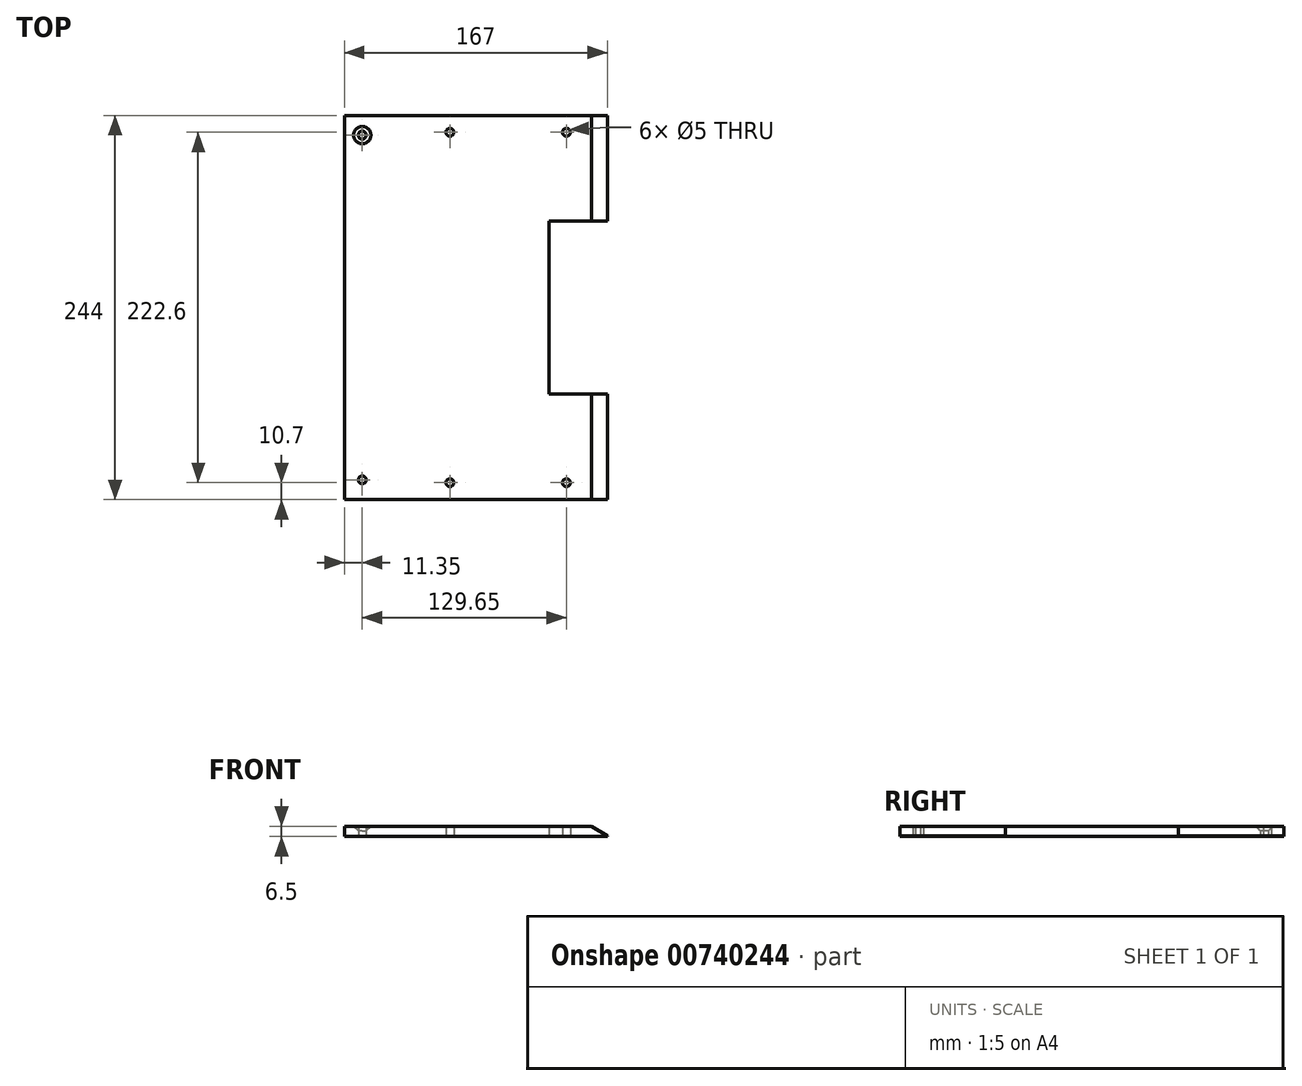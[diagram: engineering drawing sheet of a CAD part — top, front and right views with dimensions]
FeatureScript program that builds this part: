
annotation { "Feature Type Name" : "Feature", "Feature Type Description" : "" }
export const myFeature = defineFeature(function(context is Context, id is Id, definition is map)
    precondition{}
    {
        {
            var Q0;
            Q0=qCreatedBy(makeId("Top.planeOp"),FACE);
            var sketch = newSketch(context, id + "F0", { "sketchPlane" : qUnion([Q0])});
            skLineSegment(sketch, "E0.bottom", {"start": v(-120, 81) * mm, "end": v(-55, 81) * mm});
            skLineSegment(sketch, "E0.top", {"start": v(-120, -81) * mm, "end": v(120, -81) * mm});
            skLineSegment(sketch, "E0.left", {"start": v(-120, 81) * mm, "end": v(-120, -81) * mm});
            skLineSegment(sketch, "E0.right", {"start": v(120, 81) * mm, "end": v(120, -81) * mm});
            skLineSegment(sketch, "E1", {"start": v(-109, 81) * mm, "end": v(-109, -81) * mm, "construction": true});
            skLineSegment(sketch, "E2", {"start": v(109, 81) * mm, "end": v(109, -81) * mm, "construction": true});
            skCircle(sketch, "E3", {"center": v(-109, -74.65) * mm, "radius": 2.5 * mm});
            skCircle(sketch, "E4", {"center": v(-109, -19) * mm, "radius": 2.5 * mm});
            skCircle(sketch, "E5", {"center": v(-109, 55) * mm, "radius": 2.5 * mm});
            skCircle(sketch, "E6.MirrorC", {"center": v(109, 55) * mm, "radius": 2.5 * mm});
            skCircle(sketch, "E7.MirrorC", {"center": v(109, -19) * mm, "radius": 2.5 * mm});
            skCircle(sketch, "E8.MirrorC", {"center": v(109, -74.65) * mm, "radius": 2.5 * mm});
            skLineSegment(sketch, "E9.top", {"start": v(-55, 44) * mm, "end": v(55, 44) * mm});
            skLineSegment(sketch, "E9.left", {"start": v(-55, 81) * mm, "end": v(-55, 44) * mm});
            skLineSegment(sketch, "E9.right", {"start": v(55, 81) * mm, "end": v(55, 44) * mm});
            skLineSegment(sketch, "E10.trimOffspring", {"start": v(55, 81) * mm, "end": v(120, 81) * mm});
            skSolve(sketch);
        }
        {
            var Q0;
            Q0=qCreatedBy(makeId("Top.planeOp"),FACE);
            cPlane(context, id + "F1", {"entities" : qUnion([Q0]), "cplaneType" : CPlaneType.OFFSET, "offset" : 3.25 * mm, "width" : 150 * mm, "height" : 150 * mm});
        }
        {
            var Q0;
            Q0=qCreatedBy(id+"F1.planeOp",FACE);
            var sketch = newSketch(context, id + "F2", { "sketchPlane" : qUnion([Q0])});
            skLineSegment(sketch, "E11.0", {"start": v(-120, -81) * mm, "end": v(120, -81) * mm});
            skLineSegment(sketch, "E12.0", {"start": v(-120, 81) * mm, "end": v(-120, -81) * mm});
            skPoint(sketch, "E13.0", {"position": v(-87.5, 81) * mm});
            skLineSegment(sketch, "E14.0", {"start": v(-120, 81) * mm, "end": v(-55, 81) * mm});
            skLineSegment(sketch, "E15.0", {"start": v(-55, 81) * mm, "end": v(-55, 44) * mm});
            skLineSegment(sketch, "E16.0", {"start": v(-55, 44) * mm, "end": v(55, 44) * mm});
            skLineSegment(sketch, "E17.0", {"start": v(55, 81) * mm, "end": v(55, 44) * mm});
            skLineSegment(sketch, "E18.0", {"start": v(55, 81) * mm, "end": v(120, 81) * mm});
            skLineSegment(sketch, "E19.0", {"start": v(120, 81) * mm, "end": v(120, -81) * mm});
            skCircle(sketch, "E20.0", {"center": v(-109, 55) * mm, "radius": 2.5 * mm, "construction": true});
            skCircle(sketch, "E21.0", {"center": v(-109, -19) * mm, "radius": 2.5 * mm, "construction": true});
            skCircle(sketch, "E22.0", {"center": v(-109, -74.65) * mm, "radius": 2.5 * mm, "construction": true});
            skCircle(sketch, "E23.0", {"center": v(109, -74.65) * mm, "radius": 2.5 * mm, "construction": true});
            skCircle(sketch, "E24.0", {"center": v(109, -19) * mm, "radius": 2.5 * mm, "construction": true});
            skCircle(sketch, "E25.0", {"center": v(109, 55) * mm, "radius": 2.5 * mm, "construction": true});
            skCircle(sketch, "E26", {"center": v(-109, 55) * mm, "radius": 5.25 * mm});
            skCircle(sketch, "E27", {"center": v(-109, -19) * mm, "radius": 5.25 * mm});
            skCircle(sketch, "E28", {"center": v(-109, -74.65) * mm, "radius": 5.25 * mm});
            skCircle(sketch, "E29", {"center": v(109, -74.65) * mm, "radius": 5.25 * mm});
            skCircle(sketch, "E30", {"center": v(109, -19) * mm, "radius": 5.25 * mm});
            skCircle(sketch, "E31", {"center": v(109, 55) * mm, "radius": 5.25 * mm});
            skSolve(sketch);
        }
        {
            var Q0;
            Q0=qCreatedBy(makeId("Top.planeOp"),FACE);
            var sketch = newSketch(context, id + "F3", { "sketchPlane" : qUnion([Q0])});
            skLineSegment(sketch, "E32.0", {"start": v(-120, 81) * mm, "end": v(-120, -81) * mm});
            skLineSegment(sketch, "E33.0", {"start": v(-120, 81) * mm, "end": v(-55, 81) * mm});
            skLineSegment(sketch, "E34.0", {"start": v(-55, 81) * mm, "end": v(-55, 44) * mm});
            skLineSegment(sketch, "E35.0", {"start": v(-55, 44) * mm, "end": v(55, 44) * mm});
            skLineSegment(sketch, "E36.0", {"start": v(55, 81) * mm, "end": v(55, 44) * mm});
            skLineSegment(sketch, "E37.0", {"start": v(55, 81) * mm, "end": v(120, 81) * mm});
            skLineSegment(sketch, "E38.0", {"start": v(120, 81) * mm, "end": v(120, -81) * mm});
            skLineSegment(sketch, "E39.0", {"start": v(-120, -81) * mm, "end": v(120, -81) * mm});
            skSolve(sketch);
        }
        {
            var Q0;
            Q0 = qSketchRegion(id + "F3", true);
            extrude(context, id + "F4", {"entities" : qUnion([Q0]), "depth" : 6.5 * mm, "offsetDistance" : 25 * mm});
        }
        {
            var Q0;
            Q0=makeQuery(id+"F4.opExtrude","CAP_FACE",FACE,{"disambiguationData":[OSD([sQuery(id+"F3.wireOp",EDGE,"E32.0"),sQuery(id+"F3.wireOp",EDGE,"E33.0"),sQuery(id+"F3.wireOp",EDGE,"E34.0"),sQuery(id+"F3.wireOp",EDGE,"E35.0"),sQuery(id+"F3.wireOp",EDGE,"E36.0"),sQuery(id+"F3.wireOp",EDGE,"E37.0"),sQuery(id+"F3.wireOp",EDGE,"E38.0"),sQuery(id+"F3.wireOp",EDGE,"E39.0")])],"isStart":true});
            var sketch = newSketch(context, id + "F5", { "sketchPlane" : qUnion([Q0])});
            skLineSegment(sketch, "E40.0.0", {"start": v(-120, 81) * mm, "end": v(-120, -81) * mm});
            skLineSegment(sketch, "E40.0.1", {"start": v(-120, -81) * mm, "end": v(-55, -81) * mm});
            skLineSegment(sketch, "E40.0.2", {"start": v(-55, -81) * mm, "end": v(-55, -44) * mm});
            skLineSegment(sketch, "E40.0.3", {"start": v(-55, -44) * mm, "end": v(55, -44) * mm});
            skLineSegment(sketch, "E40.0.4", {"start": v(55, -44) * mm, "end": v(55, -81) * mm});
            skLineSegment(sketch, "E40.0.5", {"start": v(55, -81) * mm, "end": v(120, -81) * mm});
            skLineSegment(sketch, "E40.0.6", {"start": v(120, -81) * mm, "end": v(120, 81) * mm});
            skLineSegment(sketch, "E40.0.7", {"start": v(120, 81) * mm, "end": v(-120, 81) * mm});
            skSolve(sketch);
        }
        {
            var Q0;
            Q0=makeQuery(id+"F5.imprint","IMPRINT",FACE,{"disambiguationData":[TD([[makeQuery(id+"F5.imprint","IMPRINT",EDGE,{"derivedFrom":sQuery(id+"F5.wireOp",EDGE,"E40.0.0")}),-1.0]])]});
            var sketch = newSketch(context, id + "F6", { "sketchPlane" : qUnion([Q0])});
            skLineSegment(sketch, "E41.0", {"start": v(120, -81) * mm, "end": v(120, 81) * mm, "construction": true});
            skLineSegment(sketch, "E42.0", {"start": v(-120, 81) * mm, "end": v(-120, -81) * mm, "construction": true});
            skCircle(sketch, "E43.0", {"center": v(-109.5, 74.65) * mm, "radius": 2.5 * mm});
            skLineSegment(sketch, "E44", {"start": v(110.8, -62.03) * mm, "end": v(110.8, 48.78) * mm, "construction": true});
            skCircle(sketch, "E45", {"center": v(-111.3, 19) * mm, "radius": 2.5 * mm});
            skCircle(sketch, "E46", {"center": v(-111.3, -55) * mm, "radius": 2.5 * mm});
            skCircle(sketch, "E47", {"center": v(109.5, 74.65) * mm, "radius": 2.5 * mm});
            skCircle(sketch, "E48", {"center": v(111.3, 19) * mm, "radius": 2.5 * mm});
            skCircle(sketch, "E49", {"center": v(111.3, -55) * mm, "radius": 2.5 * mm});
            skSolve(sketch);
        }
        {
            var Q0;
            Q0 = qSketchRegion(id + "F6", true);
            extrude(context, id + "F7", {"entities" : qUnion([Q0]), "operationType" : NewBodyOperationType.REMOVE, "oppositeDirection" : true, "depth" : 25 * mm, "offsetDistance" : 25 * mm});
        }
        {
            var Q0;
            Q0=makeQuery(id+"F7.boolean.opBoolean","INTERSECT",EDGE,{"derivedFrom":[makeQuery(id+"F4.opExtrude","CAP_FACE",FACE,{"disambiguationData":[OSD([sQuery(id+"F3.wireOp",EDGE,"E32.0"),sQuery(id+"F3.wireOp",EDGE,"E33.0"),sQuery(id+"F3.wireOp",EDGE,"E34.0"),sQuery(id+"F3.wireOp",EDGE,"E35.0"),sQuery(id+"F3.wireOp",EDGE,"E36.0"),sQuery(id+"F3.wireOp",EDGE,"E37.0"),sQuery(id+"F3.wireOp",EDGE,"E38.0"),sQuery(id+"F3.wireOp",EDGE,"E39.0")])],"isStart":false}),makeQuery(id+"F7.opExtrude","SWEPT_FACE",FACE,{"disambiguationData":[OSD([sQuery(id+"F6.wireOp",EDGE,"4a9d965a-7110-4ea6-94aa-3877e39495fb0.MirrorC")])]})]});
            var Q1;
            Q1=makeQuery(id+"F7.boolean.opBoolean","INTERSECT",EDGE,{"derivedFrom":[makeQuery(id+"F4.opExtrude","CAP_FACE",FACE,{"disambiguationData":[OSD([sQuery(id+"F3.wireOp",EDGE,"E32.0"),sQuery(id+"F3.wireOp",EDGE,"E33.0"),sQuery(id+"F3.wireOp",EDGE,"E34.0"),sQuery(id+"F3.wireOp",EDGE,"E35.0"),sQuery(id+"F3.wireOp",EDGE,"E36.0"),sQuery(id+"F3.wireOp",EDGE,"E37.0"),sQuery(id+"F3.wireOp",EDGE,"E38.0"),sQuery(id+"F3.wireOp",EDGE,"E39.0")])],"isStart":false}),makeQuery(id+"F7.opExtrude","SWEPT_FACE",FACE,{"disambiguationData":[OSD([sQuery(id+"F6.wireOp",EDGE,"4a9d965a-7110-4ea6-94aa-3877e39495fb1.MirrorC")])]})]});
            var Q2;
            Q2=makeQuery(id+"F7.boolean.opBoolean","INTERSECT",EDGE,{"derivedFrom":[makeQuery(id+"F4.opExtrude","CAP_FACE",FACE,{"disambiguationData":[OSD([sQuery(id+"F3.wireOp",EDGE,"E32.0"),sQuery(id+"F3.wireOp",EDGE,"E33.0"),sQuery(id+"F3.wireOp",EDGE,"E34.0"),sQuery(id+"F3.wireOp",EDGE,"E35.0"),sQuery(id+"F3.wireOp",EDGE,"E36.0"),sQuery(id+"F3.wireOp",EDGE,"E37.0"),sQuery(id+"F3.wireOp",EDGE,"E38.0"),sQuery(id+"F3.wireOp",EDGE,"E39.0")])],"isStart":false}),makeQuery(id+"F7.opExtrude","SWEPT_FACE",FACE,{"disambiguationData":[OSD([sQuery(id+"F6.wireOp",EDGE,"c3e07381-49b0-4129-85a1-3989482c5e3f.0")])]})]});
            var Q3;
            Q3=makeQuery(id+"F7.boolean.opBoolean","INTERSECT",EDGE,{"derivedFrom":[makeQuery(id+"F4.opExtrude","CAP_FACE",FACE,{"disambiguationData":[OSD([sQuery(id+"F3.wireOp",EDGE,"E32.0"),sQuery(id+"F3.wireOp",EDGE,"E33.0"),sQuery(id+"F3.wireOp",EDGE,"E34.0"),sQuery(id+"F3.wireOp",EDGE,"E35.0"),sQuery(id+"F3.wireOp",EDGE,"E36.0"),sQuery(id+"F3.wireOp",EDGE,"E37.0"),sQuery(id+"F3.wireOp",EDGE,"E38.0"),sQuery(id+"F3.wireOp",EDGE,"E39.0")])],"isStart":false}),makeQuery(id+"F7.opExtrude","SWEPT_FACE",FACE,{"disambiguationData":[OSD([sQuery(id+"F6.wireOp",EDGE,"ncoUW5WC-DxYv-2TDS-Pk2a-PzWnnyeluWa3")])]})]});
            var Q4;
            Q4=makeQuery(id+"F7.boolean.opBoolean","INTERSECT",EDGE,{"derivedFrom":[makeQuery(id+"F4.opExtrude","CAP_FACE",FACE,{"disambiguationData":[OSD([sQuery(id+"F3.wireOp",EDGE,"E32.0"),sQuery(id+"F3.wireOp",EDGE,"E33.0"),sQuery(id+"F3.wireOp",EDGE,"E34.0"),sQuery(id+"F3.wireOp",EDGE,"E35.0"),sQuery(id+"F3.wireOp",EDGE,"E36.0"),sQuery(id+"F3.wireOp",EDGE,"E37.0"),sQuery(id+"F3.wireOp",EDGE,"E38.0"),sQuery(id+"F3.wireOp",EDGE,"E39.0")])],"isStart":false}),makeQuery(id+"F7.opExtrude","SWEPT_FACE",FACE,{"disambiguationData":[OSD([sQuery(id+"F6.wireOp",EDGE,"QlHThSrt-MAP4-YxPv-jmUJ-fxpaFjOQ3Aaq")])]})]});
            var Q5;
            Q5=makeQuery(id+"F7.boolean.opBoolean","INTERSECT",EDGE,{"derivedFrom":[makeQuery(id+"F4.opExtrude","CAP_FACE",FACE,{"disambiguationData":[OSD([sQuery(id+"F3.wireOp",EDGE,"E32.0"),sQuery(id+"F3.wireOp",EDGE,"E33.0"),sQuery(id+"F3.wireOp",EDGE,"E34.0"),sQuery(id+"F3.wireOp",EDGE,"E35.0"),sQuery(id+"F3.wireOp",EDGE,"E36.0"),sQuery(id+"F3.wireOp",EDGE,"E37.0"),sQuery(id+"F3.wireOp",EDGE,"E38.0"),sQuery(id+"F3.wireOp",EDGE,"E39.0")])],"isStart":false}),makeQuery(id+"F7.opExtrude","SWEPT_FACE",FACE,{"disambiguationData":[OSD([sQuery(id+"F6.wireOp",EDGE,"E43.0")])]})]});
            chamfer(context, id + "F8", {"entities" : qUnion([Q0, Q1, Q2, Q3, Q4, Q5]), "width" : 3 * mm, "tangentPropagation" : true});
        }
        {
            var Q0;
            Q0=makeQuery(id+"F4.opExtrude","CAP_FACE",FACE,{"disambiguationData":[OSD([sQuery(id+"F3.wireOp",EDGE,"E32.0"),sQuery(id+"F3.wireOp",EDGE,"E33.0"),sQuery(id+"F3.wireOp",EDGE,"E34.0"),sQuery(id+"F3.wireOp",EDGE,"E35.0"),sQuery(id+"F3.wireOp",EDGE,"E36.0"),sQuery(id+"F3.wireOp",EDGE,"E37.0"),sQuery(id+"F3.wireOp",EDGE,"E38.0"),sQuery(id+"F3.wireOp",EDGE,"E39.0")])],"isStart":false});
            var sketch = newSketch(context, id + "F9", { "sketchPlane" : qUnion([Q0])});
            skLineSegment(sketch, "E50.0", {"start": v(120, -81) * mm, "end": v(-120, -81) * mm, "construction": true});
            skLineSegment(sketch, "E51.0", {"start": v(120, 81) * mm, "end": v(120, -81) * mm, "construction": true});
            skCircle(sketch, "E52", {"center": v(65, -1) * mm, "radius": 10.5 * mm});
            skLineSegment(sketch, "E53.0", {"start": v(-120, 81) * mm, "end": v(-55, 81) * mm, "construction": true});
            skLineSegment(sketch, "E54.0", {"start": v(-55, 44) * mm, "end": v(55, 44) * mm, "construction": true});
            skLineSegment(sketch, "E55.0", {"start": v(55, 81) * mm, "end": v(120, 81) * mm, "construction": true});
            skCircle(sketch, "E56.MirrorC", {"center": v(-65, -1) * mm, "radius": 10.5 * mm});
            skLineSegment(sketch, "E57", {"start": v(-65, -1) * mm, "end": v(-80.64, -1) * mm, "construction": true});
            skLineSegment(sketch, "E58", {"start": v(-65, -1) * mm, "end": v(65, -1) * mm, "construction": true});
            skSolve(sketch);
        }
        {
            var Q0;
            Q0=makeQuery(id+"F4.opExtrude","SWEPT_FACE",FACE,{"disambiguationData":[OSD([sQuery(id+"F3.wireOp",EDGE,"E32.0")])]});
            extrude(context, id + "F10", {"entities" : qUnion([Q0]), "operationType" : NewBodyOperationType.ADD, "depth" : 2 * mm, "offsetDistance" : 25 * mm});
        }
        {
            var Q0;
            Q0=makeQuery(id+"F4.opExtrude","SWEPT_FACE",FACE,{"disambiguationData":[OSD([sQuery(id+"F3.wireOp",EDGE,"E38.0")])]});
            extrude(context, id + "F11", {"entities" : qUnion([Q0]), "operationType" : NewBodyOperationType.ADD, "depth" : 2 * mm, "offsetDistance" : 25 * mm});
        }
        {
            var Q0;
            Q0=makeQuery(id+"F4.opExtrude","CAP_EDGE",EDGE,{"disambiguationData":[OSD([sQuery(id+"F3.wireOp",EDGE,"E33.0")])],"isStart":false});
            var Q1;
            Q1=makeQuery(id+"F4.opExtrude","CAP_EDGE",EDGE,{"disambiguationData":[OSD([sQuery(id+"F3.wireOp",EDGE,"E37.0")])],"isStart":false});
            chamfer(context, id + "F12", {"entities" : qUnion([Q0, Q1]), "chamferType" : ChamferType.TWO_OFFSETS, "width1" : 6 * mm, "oppositeDirection" : false, "width2" : 10 * mm, "tangentPropagation" : true});
        }
        {
            var Q0;
            {var subQ0=sQuery(id+"F3.wireOp",EDGE,"E39.0");Q0=makeQuery(id+"F11.boolean.opBoolean","MERGE",FACE,{"derivedFrom":[makeQuery(id+"F10.boolean.opBoolean","MERGE",FACE,{"derivedFrom":[makeQuery(id+"F4.opExtrude","SWEPT_FACE",FACE,{"disambiguationData":[OSD([subQ0])]}),makeQuery(id+"F10.opExtrude","SWEPT_FACE",FACE,{"disambiguationData":[OSD([sQuery(id+"F3.wireOp",EDGE,"E32.0"),subQ0])]})]}),makeQuery(id+"F11.opExtrude","SWEPT_FACE",FACE,{"disambiguationData":[OSD([sQuery(id+"F3.wireOp",EDGE,"E38.0"),subQ0])]})]});}
            extrude(context, id + "F13", {"entities" : qUnion([Q0]), "operationType" : NewBodyOperationType.ADD, "depth" : 5 * mm, "offsetDistance" : 25 * mm});
        }
        {
            var Q0;
            Q0=qCreatedBy(makeId("Right.planeOp"),FACE);
            var sketch = newSketch(context, id + "F14", { "sketchPlane" : qUnion([Q0])});
            skLineSegment(sketch, "E59", {"start": v(0, 0) * mm, "end": v(0, -61.15) * mm});
            skSolve(sketch);
        }
        {
            var Q0;
            Q0=makeQuery(id+"F4.opExtrude","SWEPT_BODY",BODY,{"disambiguationData":[OSD([sQuery(id+"F3.wireOp",EDGE,"E32.0"),sQuery(id+"F3.wireOp",EDGE,"E33.0"),sQuery(id+"F3.wireOp",EDGE,"E34.0"),sQuery(id+"F3.wireOp",EDGE,"E35.0"),sQuery(id+"F3.wireOp",EDGE,"E36.0"),sQuery(id+"F3.wireOp",EDGE,"E37.0"),sQuery(id+"F3.wireOp",EDGE,"E38.0"),sQuery(id+"F3.wireOp",EDGE,"E39.0")])]});
            var Q1;
            Q1=sQuery(id+"F14.wireOp",EDGE,"E59");
            transform(context, id + "F15", {"entities" : qUnion([Q0]), "transformType" : TransformType.ROTATION, "transformAxis" : qUnion([Q1]), "angle" : 90 * degree, "makeCopy" : false});
        }
        {
            var Q0;
            {var subQ0=sQuery(id+"F3.wireOp",EDGE,"E39.0");var subQ1=sQuery(id+"F3.wireOp",EDGE,"E38.0");var subQ2=sQuery(id+"F3.wireOp",EDGE,"E32.0");Q0=makeQuery(id+"F13.boolean.opBoolean","MERGE",FACE,{"derivedFrom":[makeQuery(id+"F11.boolean.opBoolean","MERGE",FACE,{"derivedFrom":[makeQuery(id+"F10.boolean.opBoolean","MERGE",FACE,{"derivedFrom":[makeQuery(id+"F4.opExtrude","CAP_FACE",FACE,{"disambiguationData":[OSD([subQ2,sQuery(id+"F3.wireOp",EDGE,"E33.0"),sQuery(id+"F3.wireOp",EDGE,"E34.0"),sQuery(id+"F3.wireOp",EDGE,"E35.0"),sQuery(id+"F3.wireOp",EDGE,"E36.0"),sQuery(id+"F3.wireOp",EDGE,"E37.0"),subQ1,subQ0])],"isStart":true}),makeQuery(id+"F10.opExtrude","SWEPT_FACE",FACE,{"disambiguationData":[OSD([subQ2]),TDD([makeQuery(id+"F4.opExtrude","CAP_EDGE",EDGE,{"disambiguationData":[OSD([subQ2])],"isStart":true})])]})]}),makeQuery(id+"F11.opExtrude","SWEPT_FACE",FACE,{"disambiguationData":[OSD([subQ1]),TDD([makeQuery(id+"F4.opExtrude","CAP_EDGE",EDGE,{"disambiguationData":[OSD([subQ1])],"isStart":true})])]})]}),makeQuery(id+"F13.opExtrude","SWEPT_FACE",FACE,{"disambiguationData":[OSD([subQ2,subQ1,subQ0]),TDD([makeQuery(id+"F11.boolean.opBoolean","MERGE",EDGE,{"derivedFrom":[makeQuery(id+"F10.boolean.opBoolean","MERGE",EDGE,{"derivedFrom":[makeQuery(id+"F4.opExtrude","CAP_EDGE",EDGE,{"disambiguationData":[OSD([subQ0])],"isStart":true}),makeQuery(id+"F10.opExtrude","SWEPT_EDGE",EDGE,{"disambiguationData":[OSD([subQ2,subQ0]),TDD([makeQuery(id+"F4.opExtrude","CAP_VERTEX",VERTEX,{"disambiguationData":[OSD([subQ2,subQ0])],"isStart":true})])]})]}),makeQuery(id+"F11.opExtrude","SWEPT_EDGE",EDGE,{"disambiguationData":[OSD([subQ1,subQ0]),TDD([makeQuery(id+"F4.opExtrude","CAP_VERTEX",VERTEX,{"disambiguationData":[OSD([subQ1,subQ0])],"isStart":true})])]})]})])]})]});}
            var sketch = newSketch(context, id + "F16", { "sketchPlane" : qUnion([Q0])});
            skCircle(sketch, "E60.0", {"center": v(-1, -65) * mm, "radius": 10.5 * mm});
            skCircle(sketch, "E61.0", {"center": v(-1, 65) * mm, "radius": 10.5 * mm});
            skSolve(sketch);
        }
        {
            var Q0;
            Q0 = qSketchRegion(id + "F16", true);
            extrude(context, id + "F17", {"entities" : qUnion([Q0]), "operationType" : NewBodyOperationType.ADD, "oppositeDirection" : true, "depth" : 4.55 * mm, "offsetDistance" : 25 * mm});
        }
    });
